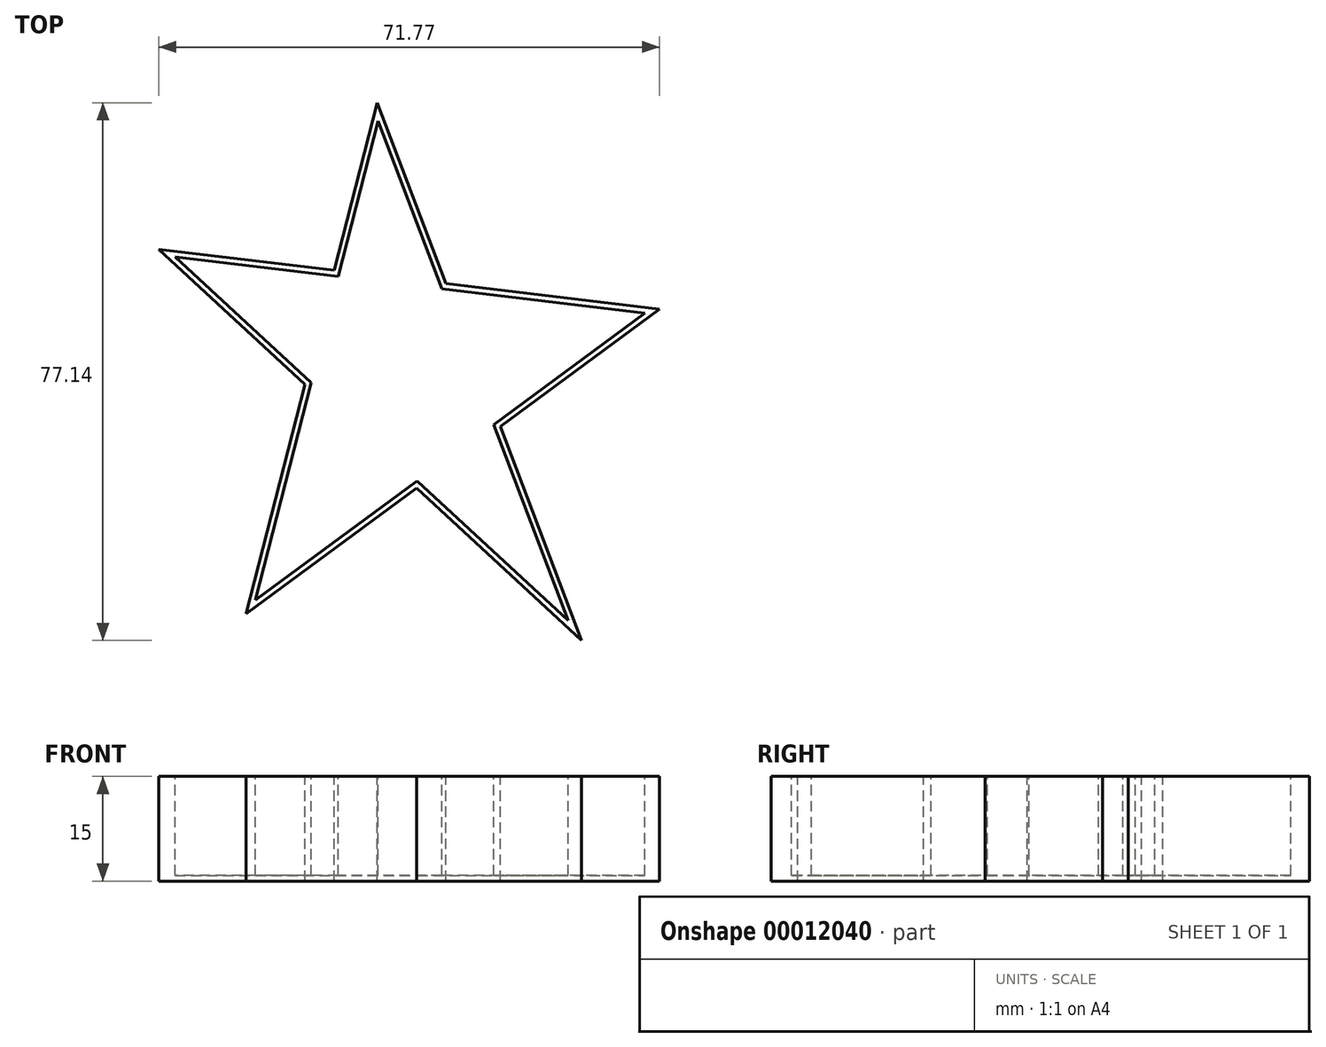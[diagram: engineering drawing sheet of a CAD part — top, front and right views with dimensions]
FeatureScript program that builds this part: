
annotation { "Feature Type Name" : "Feature", "Feature Type Description" : "" }
export const myFeature = defineFeature(function(context is Context, id is Id, definition is map)
    precondition{}
    {
        {
            var Q0;
            Q0=qCreatedBy(makeId("Top.planeOp"),FACE);
            var sketch = newSketch(context, id + "F0", { "sketchPlane" : qUnion([Q0])});
            skLineSegment(sketch, "E0", {"start": v(-7.63, 46.49) * mm, "end": v(-26.4, -26.84) * mm});
            skLineSegment(sketch, "E1", {"start": v(-26.4, -26.84) * mm, "end": v(32.85, 16.86) * mm});
            skLineSegment(sketch, "E2", {"start": v(32.85, 16.86) * mm, "end": v(-38.92, 25.46) * mm});
            skLineSegment(sketch, "E3", {"start": v(-38.92, 25.46) * mm, "end": v(21.7, -30.65) * mm});
            skLineSegment(sketch, "E4", {"start": v(21.7, -30.65) * mm, "end": v(-7.63, 46.49) * mm});
            skSolve(sketch);
        }
        {
            var Q0;
            {var subQ1=sQuery(id+"F0.wireOp",EDGE,"E2");var subQ7=sQuery(id+"F0.wireOp",EDGE,"E0");var subQ9=makeQuery(id+"F0.imprint","INTERSECT",VERTEX,{"derivedFrom":[subQ7,subQ1]});Q0=makeQuery(id+"F0.imprint","IMPRINT",FACE,{"disambiguationData":[TD([[makeQuery(id+"F0.imprint","IMPRINT",EDGE,{"disambiguationData":[TD([[subQ9,-1.0]])],"derivedFrom":subQ7}),1.0]])]});}
            var Q1;
            {var subQ0=sQuery(id+"F0.wireOp",EDGE,"E4");var subQ3=sQuery(id+"F0.wireOp",EDGE,"E0");var subQ4=makeQuery(id+"F0.imprint","INTERSECT",VERTEX,{"derivedFrom":[subQ3,subQ0]});Q1=makeQuery(id+"F0.imprint","IMPRINT",FACE,{"disambiguationData":[TD([[makeQuery(id+"F0.imprint","IMPRINT",EDGE,{"disambiguationData":[TD([[subQ4,-1.0]])],"derivedFrom":subQ3}),1.0]])]});}
            var Q2;
            {var subQ1=sQuery(id+"F0.wireOp",EDGE,"E0");var subQ3=sQuery(id+"F0.wireOp",EDGE,"E2");var subQ5=makeQuery(id+"F0.imprint","INTERSECT",VERTEX,{"derivedFrom":[subQ1,subQ3]});Q2=makeQuery(id+"F0.imprint","IMPRINT",FACE,{"disambiguationData":[TD([[makeQuery(id+"F0.imprint","IMPRINT",EDGE,{"disambiguationData":[TD([[subQ5,-1.0]])],"derivedFrom":subQ1}),-1.0]])]});}
            var Q3;
            {var subQ1=sQuery(id+"F0.wireOp",EDGE,"E1");var subQ3=sQuery(id+"F0.wireOp",EDGE,"E0");var subQ5=makeQuery(id+"F0.imprint","INTERSECT",VERTEX,{"derivedFrom":[subQ3,subQ1]});Q3=makeQuery(id+"F0.imprint","IMPRINT",FACE,{"disambiguationData":[TD([[makeQuery(id+"F0.imprint","IMPRINT",EDGE,{"disambiguationData":[TD([[subQ5,1.0]])],"derivedFrom":subQ3}),1.0]])]});}
            var Q4;
            {var subQ1=sQuery(id+"F0.wireOp",EDGE,"E1");var subQ3=sQuery(id+"F0.wireOp",EDGE,"E3");var subQ5=makeQuery(id+"F0.imprint","INTERSECT",VERTEX,{"derivedFrom":[subQ1,subQ3]});Q4=makeQuery(id+"F0.imprint","IMPRINT",FACE,{"disambiguationData":[TD([[makeQuery(id+"F0.imprint","IMPRINT",EDGE,{"disambiguationData":[TD([[subQ5,-1.0]])],"derivedFrom":subQ1}),-1.0]])]});}
            var Q5;
            {var subQ1=sQuery(id+"F0.wireOp",EDGE,"E2");var subQ3=sQuery(id+"F0.wireOp",EDGE,"E1");var subQ5=makeQuery(id+"F0.imprint","INTERSECT",VERTEX,{"derivedFrom":[subQ3,subQ1]});Q5=makeQuery(id+"F0.imprint","IMPRINT",FACE,{"disambiguationData":[TD([[makeQuery(id+"F0.imprint","IMPRINT",EDGE,{"disambiguationData":[TD([[subQ5,1.0]])],"derivedFrom":subQ3}),1.0]])]});}
            extrude(context, id + "F1", {"entities" : qUnion([Q0, Q1, Q2, Q3, Q4, Q5]), "oppositeDirection" : true, "depth" : 15 * mm});
        }
        {
            var Q0;
            Q0=makeQuery(id+"F1.opExtrude","CAP_FACE",FACE,{"disambiguationData":[OSD([sQuery(id+"F0.wireOp",EDGE,"E0"),sQuery(id+"F0.wireOp",EDGE,"E1"),sQuery(id+"F0.wireOp",EDGE,"E2"),sQuery(id+"F0.wireOp",EDGE,"E3"),sQuery(id+"F0.wireOp",EDGE,"E4")])],"isStart":true});
            shell(context, id + "F2", {"entities" : qUnion([Q0]), "thickness" : .8 * mm});
        }
    });
